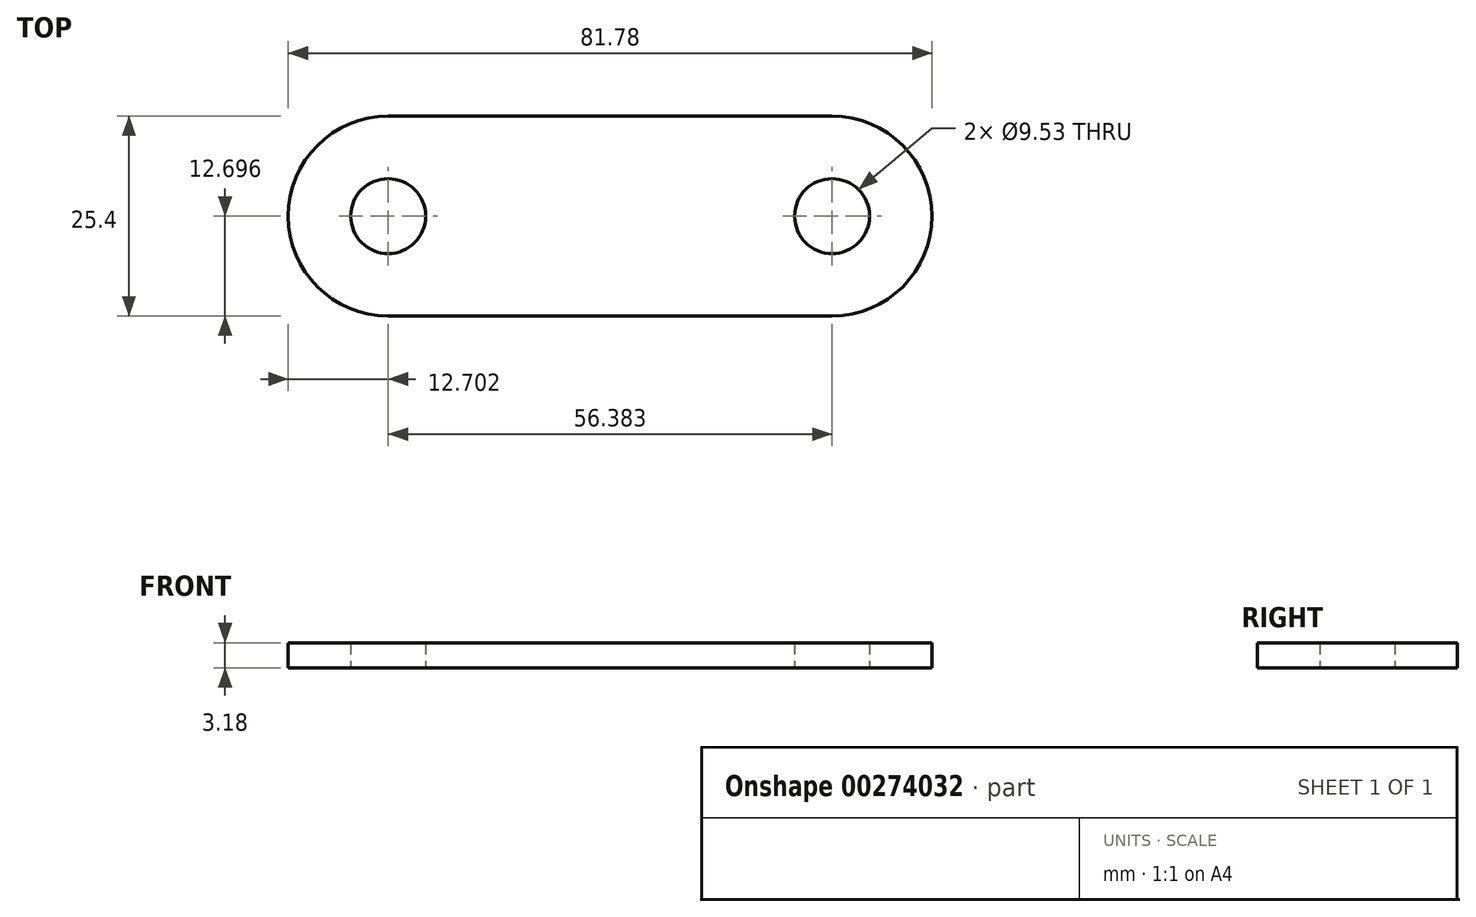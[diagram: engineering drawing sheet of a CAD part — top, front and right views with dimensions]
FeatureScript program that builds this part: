
annotation { "Feature Type Name" : "Feature", "Feature Type Description" : "" }
export const myFeature = defineFeature(function(context is Context, id is Id, definition is map)
    precondition{}
    {
        {
            var Q0;
            Q0=qCreatedBy(makeId("Top.planeOp"),FACE);
            var sketch = newSketch(context, id + "F0", { "sketchPlane" : qUnion([Q0])});
            skCircle(sketch, "E0", {"center": v(-65.6, 0.17) * mm, "radius": 4.76 * mm});
            skCircle(sketch, "E1", {"center": v(-9.22, 0.17) * mm, "radius": 4.76 * mm});
            skArc(sketch, "E2", {"start": v(-65.6, 12.87) * mm, "mid": v(-78.3, 0.17) * mm, "end": v(-65.6, -12.53) * mm});
            skArc(sketch, "E3", {"start": v(-9.22, -12.53) * mm, "mid": v(3.48, 0.17) * mm, "end": v(-9.22, 12.87) * mm});
            skLineSegment(sketch, "E4", {"start": v(-9.22, 12.87) * mm, "end": v(-65.6, 12.87) * mm});
            skLineSegment(sketch, "E5", {"start": v(-65.6, -12.53) * mm, "end": v(-9.22, -12.53) * mm});
            skPoint(sketch, "E6.trimOffspring.end.orphan", {"position": v(-65.6, 4.93) * mm});
            skPoint(sketch, "E7.start.orphan", {"position": v(-65.6, -4.6) * mm});
            skPoint(sketch, "E8.start.orphan", {"position": v(-9.22, 4.93) * mm});
            skSolve(sketch);
        }
        {
            var Q0;
            Q0 = qSketchRegion(id + "F0", true);
            extrude(context, id + "F1", {"entities" : qUnion([Q0]), "depth" : 3.17 * mm});
        }
    });
